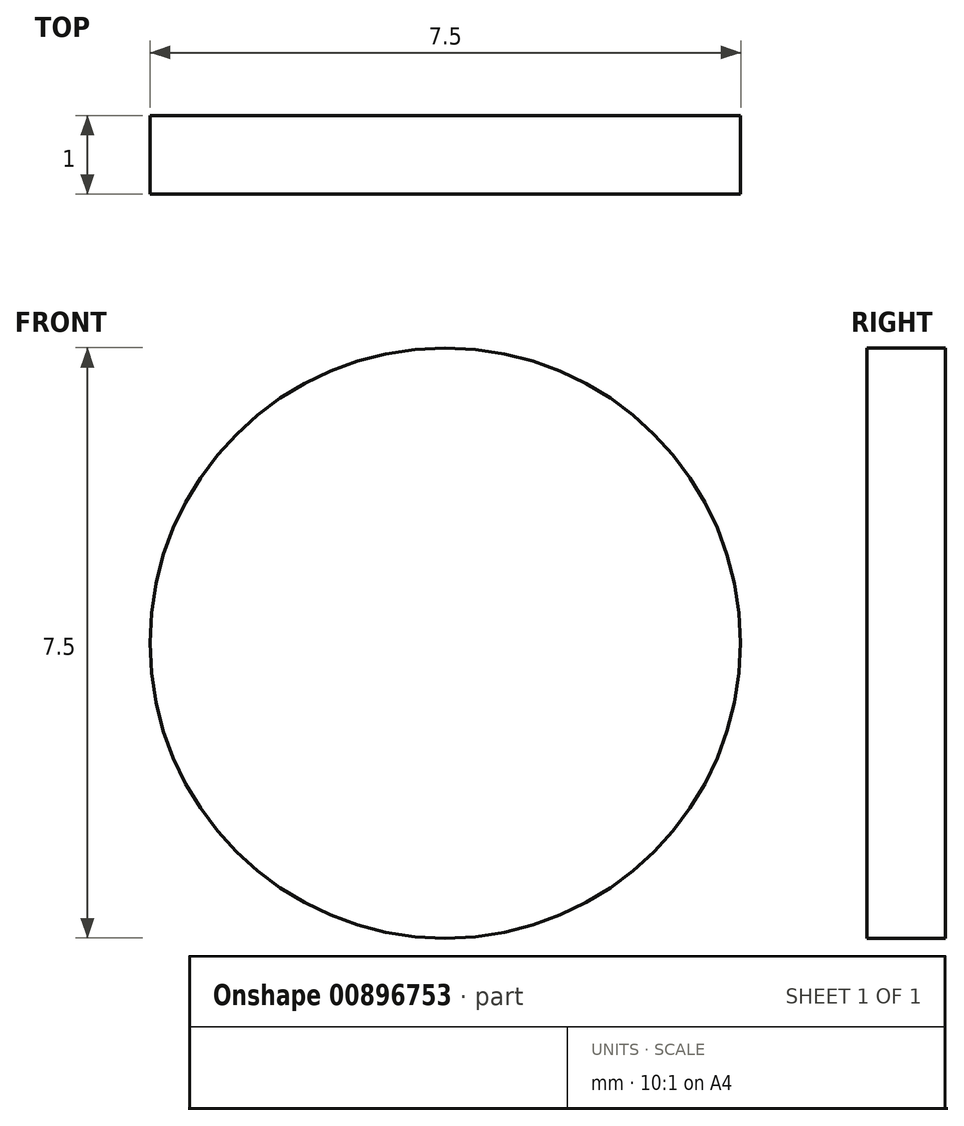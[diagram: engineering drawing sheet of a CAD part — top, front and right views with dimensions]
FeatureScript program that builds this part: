
annotation { "Feature Type Name" : "Feature", "Feature Type Description" : "" }
export const myFeature = defineFeature(function(context is Context, id is Id, definition is map)
    precondition{}
    {
        {
            var Q0;
            Q0=qCreatedBy(makeId("Front.planeOp"),FACE);
            var sketch = newSketch(context, id + "F0", { "sketchPlane" : qUnion([Q0])});
            skCircle(sketch, "E0", {"center": v(-32.77, 14.44) * mm, "radius": 3.75 * mm});
            skSolve(sketch);
        }
        {
            var Q0;
            Q0=makeQuery(id+"F0.imprint","IMPRINT",FACE,{"disambiguationData":[TD([[makeQuery(id+"F0.imprint","IMPRINT",EDGE,{"derivedFrom":sQuery(id+"F0.wireOp",EDGE,"E0")}),1.0]])]});
            extrude(context, id + "F1", {"entities" : qUnion([Q0]), "depth" : 1 * mm, "offsetDistance" : 25 * mm});
        }
    });
